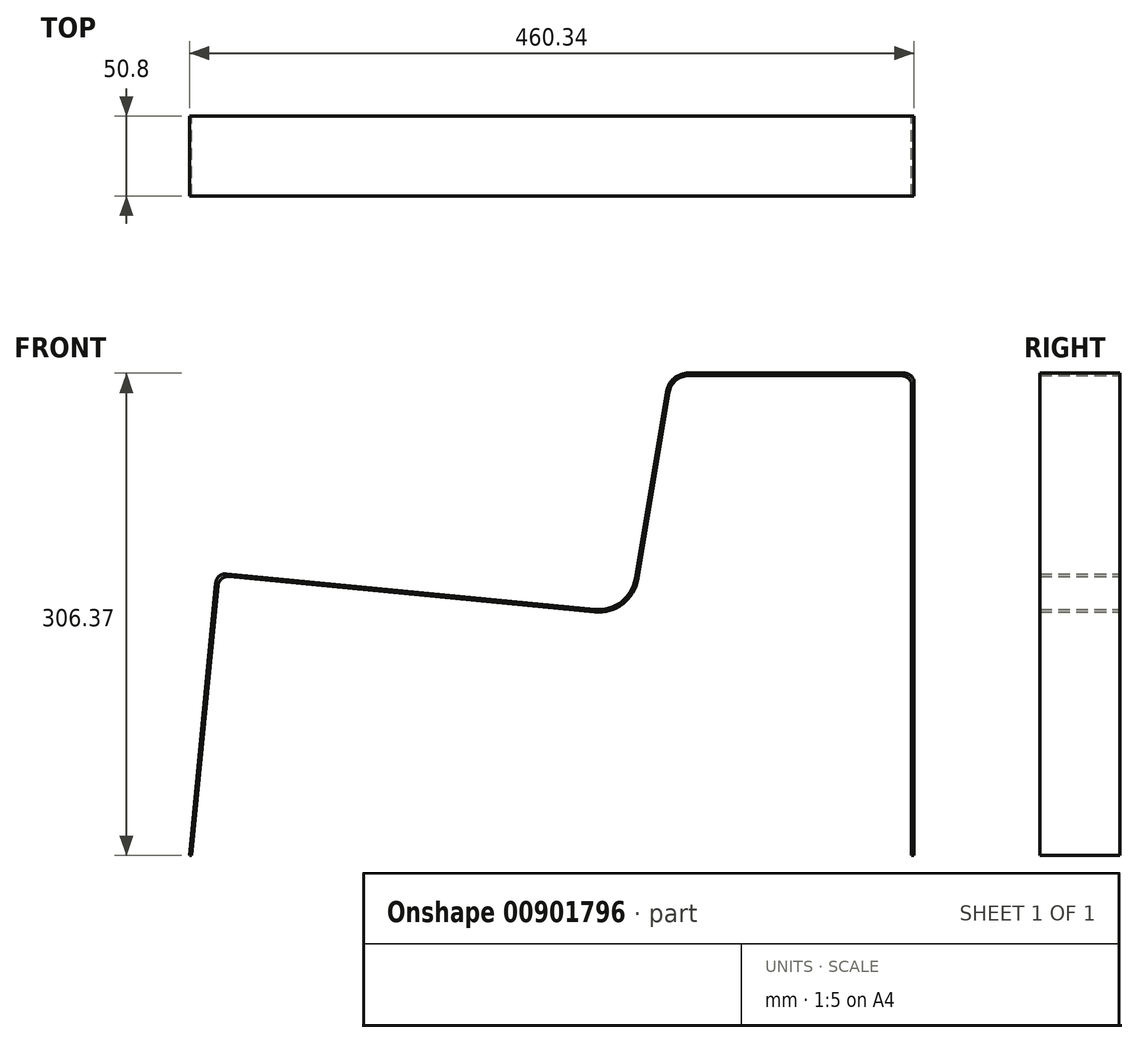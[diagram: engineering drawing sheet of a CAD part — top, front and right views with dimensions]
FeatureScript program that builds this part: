
annotation { "Feature Type Name" : "Feature", "Feature Type Description" : "" }
export const myFeature = defineFeature(function(context is Context, id is Id, definition is map)
    precondition{}
    {
        {
            var Q0;
            Q0=qCreatedBy(makeId("Front.planeOp"),FACE);
            var sketch = newSketch(context, id + "F0", { "sketchPlane" : qUnion([Q0])});
            skLineSegment(sketch, "E0", {"start": v(0, 0) * mm, "end": v(16.61, 171.48) * mm});
            skLineSegment(sketch, "E1", {"start": v(23.55, 177.19) * mm, "end": v(255.8, 154.69) * mm});
            skLineSegment(sketch, "E2", {"start": v(283.3, 175.8) * mm, "end": v(303.03, 294.19) * mm});
            skLineSegment(sketch, "E3", {"start": v(315.56, 304.8) * mm, "end": v(450.85, 304.8) * mm});
            skLineSegment(sketch, "E4", {"start": v(457.2, 298.45) * mm, "end": v(457.2, 0) * mm});
            skPoint(sketch, "E5.visualSharp", {"position": v(279.4, 152.4) * mm});
            skArc(sketch, "E5.filletArc", {"start": v(255.8, 154.69) * mm, "mid": v(273.7, 159.82) * mm, "end": v(283.3, 175.8) * mm});
            skPoint(sketch, "E6.visualSharp", {"position": v(304.8, 304.8) * mm});
            skArc(sketch, "E6.filletArc", {"start": v(315.56, 304.8) * mm, "mid": v(307.35, 301.8) * mm, "end": v(303.03, 294.19) * mm});
            skLineSegment(sketch, "E7.0", {"start": v(458.77, 300.02) * mm, "end": v(458.77, 0) * mm});
            skLineSegment(sketch, "E7.1", {"start": v(315.56, 306.37) * mm, "end": v(452.42, 306.37) * mm});
            skArc(sketch, "E7.2", {"start": v(315.56, 306.37) * mm, "mid": v(306.33, 303) * mm, "end": v(301.48, 294.45) * mm});
            skLineSegment(sketch, "E7.3", {"start": v(-1.57, 0.15) * mm, "end": v(15.2, 173.2) * mm});
            skLineSegment(sketch, "E7.4", {"start": v(22.13, 178.9) * mm, "end": v(255.95, 156.25) * mm});
            skArc(sketch, "E7.5", {"start": v(255.95, 156.25) * mm, "mid": v(272.75, 161.07) * mm, "end": v(281.75, 176.05) * mm});
            skLineSegment(sketch, "E7.6", {"start": v(281.75, 176.05) * mm, "end": v(301.48, 294.45) * mm});
            skLineSegment(sketch, "E8", {"start": v(-1.57, 0.15) * mm, "end": v(0, 0) * mm});
            skLineSegment(sketch, "E9", {"start": v(458.77, 0) * mm, "end": v(457.2, 0) * mm});
            skPoint(sketch, "E10.visualSharp", {"position": v(457.2, 304.8) * mm});
            skArc(sketch, "E10.filletArc", {"start": v(457.2, 298.45) * mm, "mid": v(455.34, 302.94) * mm, "end": v(450.85, 304.8) * mm});
            skPoint(sketch, "E11.visualSharp", {"position": v(458.77, 306.37) * mm});
            skArc(sketch, "E11.filletArc", {"start": v(458.77, 300.02) * mm, "mid": v(456.91, 304.51) * mm, "end": v(452.42, 306.37) * mm});
            skPoint(sketch, "E12.visualSharp", {"position": v(17.23, 177.8) * mm});
            skArc(sketch, "E12.filletArc", {"start": v(23.55, 177.19) * mm, "mid": v(18.9, 175.77) * mm, "end": v(16.61, 171.48) * mm});
            skPoint(sketch, "E13.visualSharp", {"position": v(15.81, 179.52) * mm});
            skArc(sketch, "E13.filletArc", {"start": v(22.13, 178.9) * mm, "mid": v(17.48, 177.49) * mm, "end": v(15.2, 173.2) * mm});
            skSolve(sketch);
        }
        {
            var Q0;
            Q0 = qSketchRegion(id + "F0", true);
            extrude(context, id + "F1", {"entities" : qUnion([Q0]), "depth" : 25.4 * mm, "offsetDistance" : 25.4 * mm, "hasSecondDirection" : true, "secondDirectionOppositeDirection" : true, "secondDirectionDepth" : 25.4 * mm});
        }
    });
